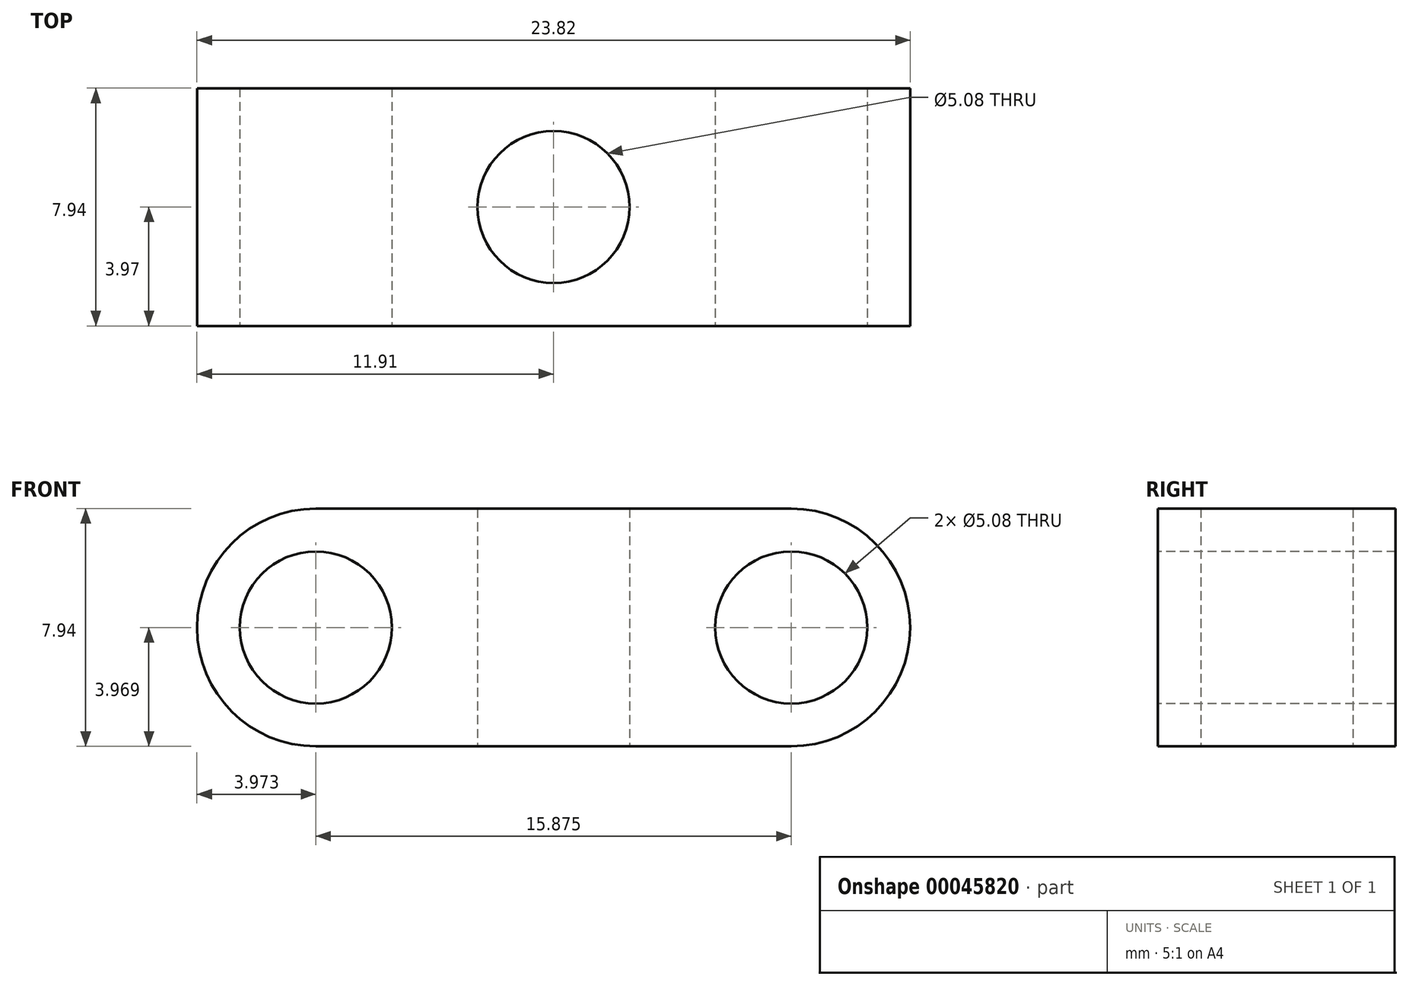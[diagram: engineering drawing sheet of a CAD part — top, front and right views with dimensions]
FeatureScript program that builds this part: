
annotation { "Feature Type Name" : "Feature", "Feature Type Description" : "" }
export const myFeature = defineFeature(function(context is Context, id is Id, definition is map)
    precondition{}
    {
        {
            var Q0;
            Q0=qCreatedBy(makeId("Top.planeOp"),FACE);
            var sketch = newSketch(context, id + "F0", { "sketchPlane" : qUnion([Q0])});
            skLineSegment(sketch, "E0.rect.bottom", {"start": v(11.9, -3.97) * mm, "end": v(-11.9, -3.97) * mm});
            skLineSegment(sketch, "E0.rect.top", {"start": v(11.9, 3.97) * mm, "end": v(-11.9, 3.97) * mm});
            skLineSegment(sketch, "E0.rect.left", {"start": v(11.9, -3.97) * mm, "end": v(11.9, 3.97) * mm});
            skLineSegment(sketch, "E0.rect.right", {"start": v(-11.9, -3.97) * mm, "end": v(-11.9, 3.97) * mm});
            skPoint(sketch, "E0.rect.middle", {"position": v(0, 0) * mm});
            skCircle(sketch, "E1", {"center": v(0, 0) * mm, "radius": 2.54 * mm});
            skSolve(sketch);
        }
        {
            var Q0;
            Q0=qSketchRegion(id+"F0",true);
            extrude(context, id + "F1", {"entities" : qUnion([Q0]), "depth" : 7.94 * mm});
        }
        {
            var Q0;
            Q0=makeQuery(id+"F1.opExtrude","SWEPT_FACE",FACE,{"disambiguationData":[OSD([sQuery(id+"F0.wireOp",EDGE,"E0.rect.bottom")])]});
            var sketch = newSketch(context, id + "F2", { "sketchPlane" : qUnion([Q0])});
            skLineSegment(sketch, "E2", {"start": v(-11.9, 3.97) * mm, "end": v(-7.94, 3.97) * mm});
            skLineSegment(sketch, "E3", {"start": v(-7.94, 3.97) * mm, "end": v(7.94, 3.97) * mm});
            skLineSegment(sketch, "E4", {"start": v(7.94, 3.97) * mm, "end": v(11.9, 3.97) * mm});
            skCircle(sketch, "E5", {"center": v(-7.94, 3.97) * mm, "radius": 2.54 * mm});
            skCircle(sketch, "E6", {"center": v(7.94, 3.97) * mm, "radius": 2.54 * mm});
            skSolve(sketch);
        }
        {
            var Q0;
            Q0=qSketchRegion(id+"F2",true);
            var Q1;
            Q1=makeQuery(id+"F1.opExtrude","SWEPT_FACE",FACE,{"disambiguationData":[OSD([sQuery(id+"F0.wireOp",EDGE,"E0.rect.top")])]});
            extrude(context, id + "F3", {"entities" : qUnion([Q0]), "operationType" : NewBodyOperationType.REMOVE, "endBound" : BoundingType.UP_TO_SURFACE, "oppositeDirection" : true, "endBoundEntityFace" : qUnion([Q1]), "depth" : 25.4 * mm});
        }
        {
            var Q0;
            Q0=makeQuery(id+"F1.opExtrude","CAP_EDGE",EDGE,{"disambiguationData":[OSD([sQuery(id+"F0.wireOp",EDGE,"E0.rect.left")])],"isStart":false});
            var Q1;
            Q1=makeQuery(id+"F1.opExtrude","CAP_EDGE",EDGE,{"disambiguationData":[OSD([sQuery(id+"F0.wireOp",EDGE,"E0.rect.left")])],"isStart":true});
            var Q2;
            Q2=makeQuery(id+"F1.opExtrude","CAP_EDGE",EDGE,{"disambiguationData":[OSD([sQuery(id+"F0.wireOp",EDGE,"E0.rect.right")])],"isStart":false});
            var Q3;
            Q3=makeQuery(id+"F1.opExtrude","CAP_EDGE",EDGE,{"disambiguationData":[OSD([sQuery(id+"F0.wireOp",EDGE,"E0.rect.right")])],"isStart":true});
            fillet(context, id + "F4", {"entities" : qUnion([Q0, Q1, Q2, Q3]), "radius" : 3.97 * mm, "tangentPropagation" : true, "allowEdgeOverflow" : false});
        }
    });
